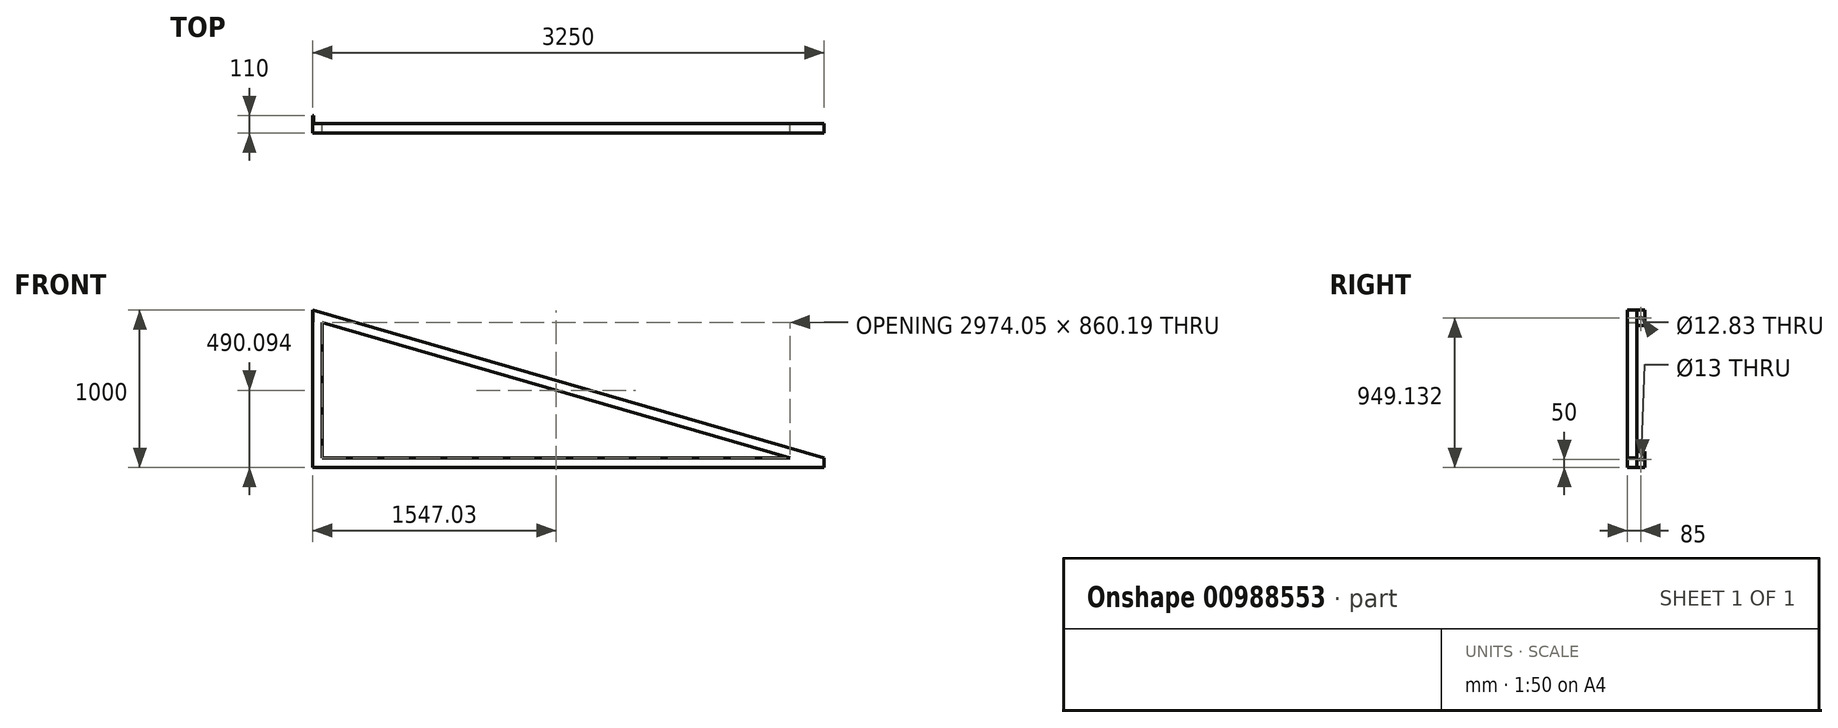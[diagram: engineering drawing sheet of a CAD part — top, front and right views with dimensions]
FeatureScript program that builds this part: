
annotation { "Feature Type Name" : "Feature", "Feature Type Description" : "" }
export const myFeature = defineFeature(function(context is Context, id is Id, definition is map)
    precondition{}
    {
        {
            var Q0;
            Q0=qCreatedBy(makeId("Front.planeOp"),FACE);
            var sketch = newSketch(context, id + "F0", { "sketchPlane" : qUnion([Q0])});
            skLineSegment(sketch, "E0", {"start": v(0, 0) * mm, "end": v(3250, 0) * mm});
            skLineSegment(sketch, "E1", {"start": v(3250, 0) * mm, "end": v(3250, 60) * mm});
            skLineSegment(sketch, "E2", {"start": v(3250, 60) * mm, "end": v(0, 1000) * mm});
            skLineSegment(sketch, "E3", {"start": v(0, 1000) * mm, "end": v(0, 0) * mm});
            skLineSegment(sketch, "E4", {"start": v(60, 60) * mm, "end": v(3034.05, 60) * mm});
            skLineSegment(sketch, "E5", {"start": v(3034.05, 60) * mm, "end": v(60, 920.19) * mm});
            skLineSegment(sketch, "E6", {"start": v(60, 920.19) * mm, "end": v(60, 60) * mm});
            skSolve(sketch);
        }
        {
            var Q0;
            Q0=makeQuery(id+"F0.imprint","IMPRINT",FACE,{"disambiguationData":[TD([[makeQuery(id+"F0.imprint","IMPRINT",EDGE,{"derivedFrom":sQuery(id+"F0.wireOp",EDGE,"E0")}),1.0]])]});
            extrude(context, id + "F1", {"entities" : qUnion([Q0]), "depth" : 60 * mm, "offsetDistance" : 25 * mm});
        }
        {
            var Q0;
            Q0=makeQuery(id+"F1.opExtrude","CAP_FACE",FACE,{"disambiguationData":[OSD([sQuery(id+"F0.wireOp",EDGE,"E0"),sQuery(id+"F0.wireOp",EDGE,"E1"),sQuery(id+"F0.wireOp",EDGE,"E2"),sQuery(id+"F0.wireOp",EDGE,"E3"),sQuery(id+"F0.wireOp",EDGE,"E4"),sQuery(id+"F0.wireOp",EDGE,"E5"),sQuery(id+"F0.wireOp",EDGE,"E6")])],"isStart":true});
            var sketch = newSketch(context, id + "F2", { "sketchPlane" : qUnion([Q0])});
            skLineSegment(sketch, "E7.bottom", {"start": v(0, 0) * mm, "end": v(-6, 0) * mm});
            skLineSegment(sketch, "E7.top", {"start": v(0, 100) * mm, "end": v(-6, 100) * mm});
            skLineSegment(sketch, "E7.left", {"start": v(0, 0) * mm, "end": v(0, 100) * mm});
            skLineSegment(sketch, "E7.right", {"start": v(-6, 0) * mm, "end": v(-6, 100) * mm});
            skSolve(sketch);
        }
        {
            var Q0;
            Q0=makeQuery(id+"F2.imprint","IMPRINT",FACE,{"disambiguationData":[TD([[makeQuery(id+"F2.imprint","IMPRINT",EDGE,{"derivedFrom":sQuery(id+"F2.wireOp",EDGE,"E7.bottom")}),-1.0]])]});
            extrude(context, id + "F3", {"entities" : qUnion([Q0]), "operationType" : NewBodyOperationType.ADD, "depth" : 50 * mm, "offsetDistance" : 25 * mm});
        }
        {
            var Q0;
            Q0=makeQuery(id+"F1.opExtrude","CAP_FACE",FACE,{"disambiguationData":[OSD([sQuery(id+"F0.wireOp",EDGE,"E0"),sQuery(id+"F0.wireOp",EDGE,"E1"),sQuery(id+"F0.wireOp",EDGE,"E2"),sQuery(id+"F0.wireOp",EDGE,"E3"),sQuery(id+"F0.wireOp",EDGE,"E4"),sQuery(id+"F0.wireOp",EDGE,"E5"),sQuery(id+"F0.wireOp",EDGE,"E6")])],"isStart":true});
            var sketch = newSketch(context, id + "F4", { "sketchPlane" : qUnion([Q0])});
            skLineSegment(sketch, "E8.bottom", {"start": v(0, 1000) * mm, "end": v(-6, 1000) * mm});
            skLineSegment(sketch, "E8.top", {"start": v(0, 900) * mm, "end": v(-6, 900) * mm});
            skLineSegment(sketch, "E8.left", {"start": v(0, 1000) * mm, "end": v(0, 900) * mm});
            skLineSegment(sketch, "E8.right", {"start": v(-6, 1000) * mm, "end": v(-6, 900) * mm});
            skSolve(sketch);
        }
        {
            var Q0;
            {var subQ0=sQuery(id+"F4.wireOp",EDGE,"E8.top");Q0=makeQuery(id+"F4.imprint","IMPRINT",FACE,{"disambiguationData":[TD([[makeQuery(id+"F4.imprint","IMPRINT",EDGE,{"derivedFrom":subQ0}),-1.0]])]});}
            extrude(context, id + "F5", {"entities" : qUnion([Q0]), "operationType" : NewBodyOperationType.ADD, "depth" : 50 * mm, "offsetDistance" : 25 * mm});
        }
        {
            var Q0;
            Q0=makeQuery(id+"F5.opExtrude","SWEPT_FACE",FACE,{"disambiguationData":[OSD([sQuery(id+"F4.wireOp",EDGE,"E8.right")])]});
            var sketch = newSketch(context, id + "F6", { "sketchPlane" : qUnion([Q0])});
            skCircle(sketch, "E9", {"center": v(25, 949.13) * mm, "radius": 6.41 * mm});
            skPoint(sketch, "E9.centerSnap0", {"position": v(25, 998.26) * mm});
            skPoint(sketch, "E9.centerSnap1", {"position": v(0, 949.13) * mm});
            skSolve(sketch);
        }
        {
            var Q0;
            Q0=makeQuery(id+"F6.imprint","IMPRINT",FACE,{"disambiguationData":[TD([[makeQuery(id+"F6.imprint","IMPRINT",EDGE,{"derivedFrom":sQuery(id+"F6.wireOp",EDGE,"E9")}),1.0]])]});
            extrude(context, id + "F7", {"entities" : qUnion([Q0]), "operationType" : NewBodyOperationType.REMOVE, "oppositeDirection" : true, "depth" : 25 * mm, "offsetDistance" : 25 * mm});
        }
        {
            var Q0;
            Q0=makeQuery(id+"F3.opExtrude","SWEPT_FACE",FACE,{"disambiguationData":[OSD([sQuery(id+"F2.wireOp",EDGE,"E7.right")])]});
            var sketch = newSketch(context, id + "F8", { "sketchPlane" : qUnion([Q0])});
            skCircle(sketch, "E10", {"center": v(25, 50) * mm, "radius": 6.5 * mm});
            skPoint(sketch, "E10.centerSnap0", {"position": v(0, 50) * mm});
            skPoint(sketch, "E10.centerSnap1", {"position": v(25, 100) * mm});
            skSolve(sketch);
        }
        {
            var Q0;
            Q0 = qSketchRegion(id + "F8", true);
            extrude(context, id + "F9", {"entities" : qUnion([Q0]), "operationType" : NewBodyOperationType.REMOVE, "oppositeDirection" : true, "depth" : 25 * mm, "offsetDistance" : 25 * mm});
        }
    });
